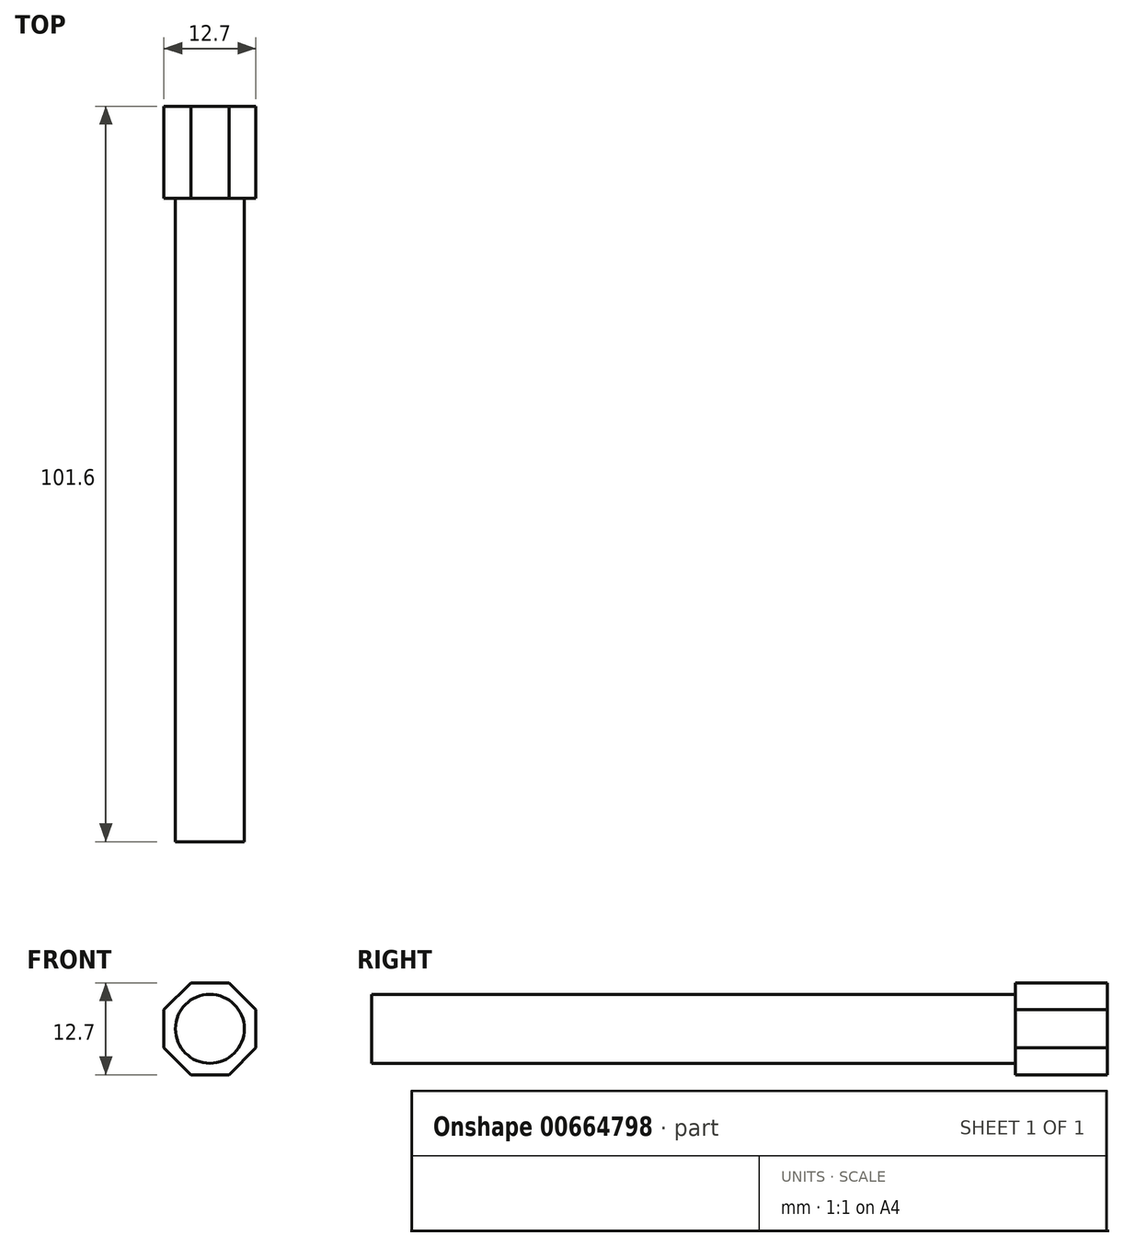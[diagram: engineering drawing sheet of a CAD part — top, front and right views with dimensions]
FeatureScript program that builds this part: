
annotation { "Feature Type Name" : "Feature", "Feature Type Description" : "" }
export const myFeature = defineFeature(function(context is Context, id is Id, definition is map)
    precondition{}
    {
        {
            var Q0;
            Q0=qCreatedBy(makeId("Front.planeOp"),FACE);
            var sketch = newSketch(context, id + "F0", { "sketchPlane" : qUnion([Q0])});
            skCircle(sketch, "E0", {"center": v(0, 0) * mm, "radius": 4.76 * mm});
            skSolve(sketch);
        }
        {
            var Q0;
            Q0 = qSketchRegion(id + "F0", true);
            extrude(context, id + "F1", {"entities" : qUnion([Q0]), "depth" : 101.6 * mm, "offsetDistance" : 25.4 * mm});
        }
        {
            var Q0;
            Q0=qCreatedBy(makeId("Front.planeOp"),FACE);
            var sketch = newSketch(context, id + "F2", { "sketchPlane" : qUnion([Q0])});
            skCircle(sketch, "E1.cCircle", {"center": v(0, 0) * mm, "radius": 6.35 * mm, "construction": true});
            skLineSegment(sketch, "E1.0", {"start": v(2.63, -6.35) * mm, "end": v(-2.63, -6.35) * mm});
            skLineSegment(sketch, "E1.1", {"start": v(-2.63, -6.35) * mm, "end": v(-6.35, -2.63) * mm});
            skLineSegment(sketch, "E1.2", {"start": v(-6.35, -2.63) * mm, "end": v(-6.35, 2.63) * mm});
            skLineSegment(sketch, "E1.3", {"start": v(-6.35, 2.63) * mm, "end": v(-2.63, 6.35) * mm});
            skLineSegment(sketch, "E1.4", {"start": v(-2.63, 6.35) * mm, "end": v(2.63, 6.35) * mm});
            skLineSegment(sketch, "E1.5", {"start": v(2.63, 6.35) * mm, "end": v(6.35, 2.63) * mm});
            skLineSegment(sketch, "E1.6", {"start": v(6.35, 2.63) * mm, "end": v(6.35, -2.63) * mm});
            skLineSegment(sketch, "E1.7", {"start": v(6.35, -2.63) * mm, "end": v(2.63, -6.35) * mm});
            skPoint(sketch, "E1.0.midPoint", {"position": v(0, -6.35) * mm});
            skSolve(sketch);
        }
        {
            var Q0;
            Q0 = qSketchRegion(id + "F2", true);
            extrude(context, id + "F3", {"entities" : qUnion([Q0]), "operationType" : NewBodyOperationType.ADD, "depth" : 12.7 * mm, "offsetDistance" : 25.4 * mm});
        }
    });
